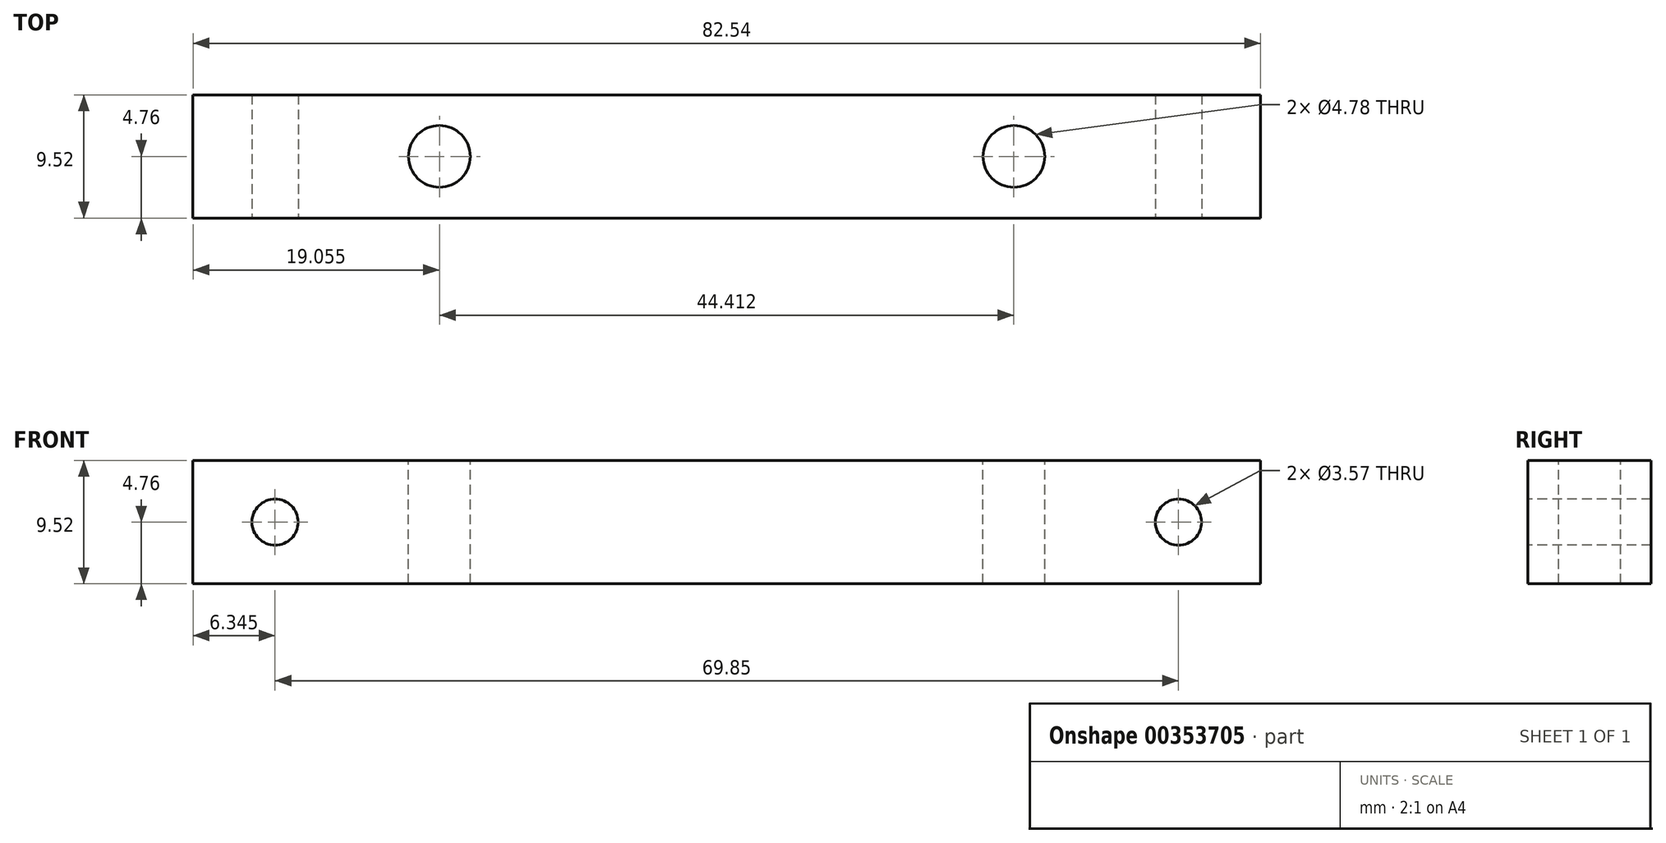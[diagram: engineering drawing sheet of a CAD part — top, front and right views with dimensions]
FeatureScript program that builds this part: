
annotation { "Feature Type Name" : "Feature", "Feature Type Description" : "" }
export const myFeature = defineFeature(function(context is Context, id is Id, definition is map)
    precondition{}
    {
        {
            var Q0;
            Q0=qCreatedBy(makeId("Front.planeOp"),FACE);
            var sketch = newSketch(context, id + "F0", { "sketchPlane" : qUnion([Q0])});
            skLineSegment(sketch, "E0.bottom", {"start": v(41.28, 4.76) * mm, "end": v(-41.28, 4.76) * mm});
            skLineSegment(sketch, "E0.top", {"start": v(41.28, -4.76) * mm, "end": v(-41.28, -4.76) * mm});
            skLineSegment(sketch, "E0.left", {"start": v(41.28, 4.76) * mm, "end": v(41.28, -4.76) * mm});
            skLineSegment(sketch, "E0.right", {"start": v(-41.28, 4.76) * mm, "end": v(-41.28, -4.76) * mm});
            skPoint(sketch, "E0.middle", {"position": v(0, 0) * mm});
            skSolve(sketch);
        }
        {
            var Q0;
            Q0 = qSketchRegion(id + "F0", true);
            extrude(context, id + "F1", {"entities" : qUnion([Q0]), "depth" : 9.52 * mm, "symmetric" : true});
        }
        {
            var Q0;
            Q0=makeQuery(id+"F1.opExtrude","CAP_FACE",FACE,{"disambiguationData":[OSD([sQuery(id+"F0.wireOp",EDGE,"E0.bottom"),sQuery(id+"F0.wireOp",EDGE,"E0.top"),sQuery(id+"F0.wireOp",EDGE,"E0.left"),sQuery(id+"F0.wireOp",EDGE,"E0.right")])],"isStart":false});
            var sketch = newSketch(context, id + "F2", { "sketchPlane" : qUnion([Q0])});
            skLineSegment(sketch, "E1", {"start": v(-41.28, 0) * mm, "end": v(-34.93, 0) * mm, "construction": true});
            skCircle(sketch, "E2", {"center": v(-34.93, 0) * mm, "radius": 1.79 * mm});
            skSolve(sketch);
        }
        {
            var Q0;
            Q0 = qSketchRegion(id + "F2", true);
            extrude(context, id + "F3", {"entities" : qUnion([Q0]), "operationType" : NewBodyOperationType.REMOVE, "oppositeDirection" : true, "depth" : 9.52 * mm});
        }
        {
            var Q0;
            Q0=makeQuery(id+"F1.opExtrude","CAP_FACE",FACE,{"disambiguationData":[OSD([sQuery(id+"F0.wireOp",EDGE,"E0.bottom"),sQuery(id+"F0.wireOp",EDGE,"E0.top"),sQuery(id+"F0.wireOp",EDGE,"E0.left"),sQuery(id+"F0.wireOp",EDGE,"E0.right")])],"isStart":false});
            var sketch = newSketch(context, id + "F4", { "sketchPlane" : qUnion([Q0])});
            skLineSegment(sketch, "E3", {"start": v(41.28, 0) * mm, "end": v(34.93, 0) * mm, "construction": true});
            skPoint(sketch, "E3.endSnap0", {"position": v(41.28, 0) * mm});
            skCircle(sketch, "E4", {"center": v(34.93, 0) * mm, "radius": 1.79 * mm});
            skSolve(sketch);
        }
        {
            var Q0;
            Q0 = qSketchRegion(id + "F4", true);
            extrude(context, id + "F5", {"entities" : qUnion([Q0]), "operationType" : NewBodyOperationType.REMOVE, "oppositeDirection" : true, "depth" : 9.52 * mm});
        }
        {
            var Q0;
            Q0=makeQuery(id+"F1.opExtrude","SWEPT_FACE",FACE,{"disambiguationData":[OSD([sQuery(id+"F0.wireOp",EDGE,"E0.bottom")])]});
            var sketch = newSketch(context, id + "F6", { "sketchPlane" : qUnion([Q0])});
            skLineSegment(sketch, "E5", {"start": v(-41.28, 0) * mm, "end": v(-22.21, 0) * mm, "construction": true});
            skPoint(sketch, "E5.endSnap0", {"position": v(-41.28, 0) * mm});
            skCircle(sketch, "E6", {"center": v(-22.21, 0) * mm, "radius": 2.39 * mm});
            skSolve(sketch);
        }
        {
            var Q0;
            {var subQ0=sQuery(id+"F0.wireOp",EDGE,"E0.bottom");Q0=makeQuery(id+"F6.imprint","IMPRINT",FACE,{"disambiguationData":[TD([[makeQuery(id+"F6.imprint","IMPRINT",EDGE,{"derivedFrom":makeQuery(id+"F1.opExtrude","CAP_EDGE",EDGE,{"disambiguationData":[OSD([subQ0])],"isStart":true})}),1.0]])]});}
            var sketch = newSketch(context, id + "F7", { "sketchPlane" : qUnion([Q0])});
            skLineSegment(sketch, "E7", {"start": v(41.25, 0) * mm, "end": v(22.2, 0) * mm, "construction": true});
            skCircle(sketch, "E8", {"center": v(22.2, 0) * mm, "radius": 2.39 * mm});
            skSolve(sketch);
        }
        {
            var Q0;
            Q0 = qSketchRegion(id + "F7", true);
            extrude(context, id + "F8", {"entities" : qUnion([Q0]), "operationType" : NewBodyOperationType.REMOVE, "oppositeDirection" : true, "depth" : 25.4 * mm});
        }
        {
            var Q0;
            Q0 = qSketchRegion(id + "F6", true);
            extrude(context, id + "F9", {"entities" : qUnion([Q0]), "operationType" : NewBodyOperationType.REMOVE, "oppositeDirection" : true, "depth" : 25.4 * mm});
        }
    });
